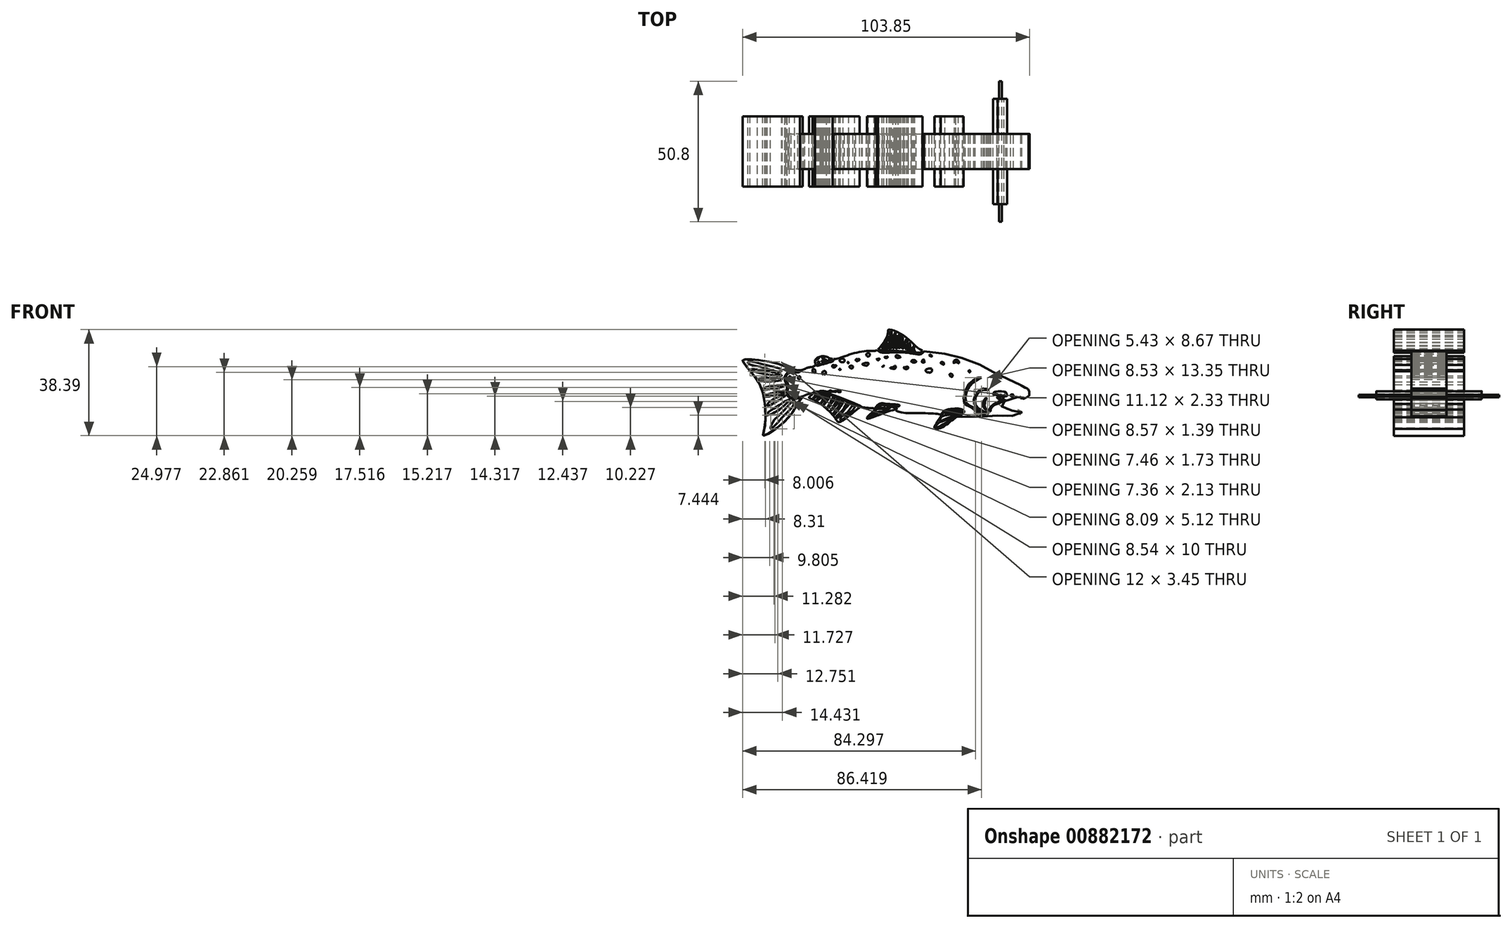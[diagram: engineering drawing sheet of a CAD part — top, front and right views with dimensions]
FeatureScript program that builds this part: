
annotation { "Feature Type Name" : "Feature", "Feature Type Description" : "" }
export const myFeature = defineFeature(function(context is Context, id is Id, definition is map)
    precondition{}
    {
        {
            var Q0;
            Q0=qCreatedBy(makeId("Front.planeOp"),FACE);
            var sketch = newSketch(context, id + "F0", { "sketchPlane" : qUnion([Q0])});
            skFitSpline(sketch, "E0", {"points": [v(-126.3, 57.16) * mm, v(-122.53, 51.96) * mm, v(-118.96, 45.5) * mm, v(-118.32, 32.67) * mm, v(-118.83, 29.86) * mm, v(-114.86, 31.9) * mm, v(-108.2, 38.29) * mm, v(-103.96, 44.3) * mm, v(-100.92, 44.95) * mm, v(-102.26, 43.7) * mm, v(-100.62, 42.85) * mm, v(-92.77, 36.26) * mm, v(-91.17, 34.8) * mm, v(-83.94, 40.08) * mm, v(-83.18, 40.16) * mm, v(-78.63, 39.71) * mm, v(-78.28, 39.56) * mm, v(-81.34, 36.1) * mm, v(-71.88, 39.13) * mm, v(-69.43, 38.37) * mm, v(-54.86, 37.46) * mm, v(-55.12, 35.97) * mm, v(-56.86, 32.59) * mm, v(-53.83, 33.01) * mm, v(-48.9, 36.64) * mm, v(-48.56, 36.58) * mm, v(-43.64, 36.74) * mm, v(-41.12, 37.23) * mm, v(-39, 36.68) * mm, v(-34.73, 37.16) * mm, v(-31.65, 36.82) * mm, v(-26.68, 37.33) * mm, v(-25.53, 37.66) * mm, v(-25.43, 38.9) * mm, v(-28.05, 39) * mm, v(-30.44, 39.16) * mm, v(-32.58, 40.43) * mm, v(-33.75, 41.28) * mm, v(-30.31, 42.82) * mm, v(-27.37, 44.06) * mm, v(-26.7, 43.54) * mm, v(-26.4, 43.85) * mm, v(-26.23, 43.54) * mm, v(-26.07, 43.6) * mm, v(-25.93, 43.87) * mm, v(-25.54, 43.76) * mm, v(-25.7, 43.55) * mm, v(-25.57, 43.34) * mm, v(-25.43, 43.29) * mm, v(-25.42, 43.53) * mm, v(-25.04, 43.51) * mm, v(-24.92, 43.25) * mm, v(-24.5, 43.23) * mm, v(-24.44, 43.36) * mm, v(-24.2, 43.37) * mm, v(-24.14, 43.56) * mm, v(-24.03, 43.54) * mm, v(-23.85, 43.56) * mm, v(-23.77, 43.75) * mm, v(-23.44, 43.71) * mm, v(-23.4, 43.9) * mm, v(-23.1, 43.92) * mm, v(-23.05, 44.05) * mm, v(-22.85, 44.1) * mm, v(-22.84, 44.24) * mm, v(-22.78, 44.3) * mm, v(-22.72, 44.39) * mm, v(-22.56, 44.46) * mm, v(-22.56, 44.68) * mm, v(-22.49, 44.73) * mm, v(-22.46, 45.17) * mm, v(-22.47, 45.89) * mm, v(-22.58, 45.95) * mm, v(-22.65, 46.15) * mm, v(-22.81, 46.18) * mm, v(-22.85, 46.49) * mm, v(-22.98, 46.5) * mm, v(-23.12, 46.57) * mm, v(-23.18, 46.78) * mm, v(-23.3, 46.81) * mm, v(-23.32, 46.9) * mm, v(-23.52, 46.9) * mm, v(-26.4, 48.49) * mm, v(-29.5, 49.94) * mm, v(-33.16, 51.55) * mm, v(-38.1, 54.14) * mm, v(-41.46, 56) * mm, v(-48.26, 58.33) * mm, v(-53.61, 59.55) * mm, v(-61.65, 60.79) * mm, v(-67.3, 65.55) * mm, v(-73.5, 68.17) * mm, v(-73.8, 66.6) * mm, v(-77.67, 60.8) * mm, v(-79.56, 60.56) * mm, v(-87.18, 59.3) * mm, v(-93.71, 57.6) * mm, v(-96.9, 58.57) * mm, v(-99.98, 57.26) * mm, v(-100.13, 55.18) * mm, v(-102.83, 54.44) * mm, v(-103.97, 53.88) * mm, v(-106.77, 53.53) * mm, v(-110.98, 54.97) * mm, v(-115.33, 56.3) * mm, v(-118.88, 56.97) * mm, v(-122.25, 57.44) * mm, v(-125.65, 57.42) * mm, v(-126.3, 57.16) * mm]});
            skFitSpline(sketch, "E1", {"points": [v(-38.58, 42.2) * mm, v(-38.49, 42.7) * mm, v(-38.1, 43.23) * mm, v(-37.98, 43.46) * mm, v(-38.38, 43.35) * mm, v(-38.98, 42.75) * mm, v(-39.22, 42.08) * mm, v(-39.2, 40.97) * mm, v(-39.1, 40.03) * mm, v(-38.17, 39.18) * mm, v(-38.49, 39.94) * mm, v(-38.76, 40.68) * mm, v(-38.58, 42.2) * mm]});
            skFitSpline(sketch, "E2", {"points": [v(-37.16, 46.3) * mm, v(-39.3, 46.36) * mm, v(-41.74, 44.47) * mm, v(-41.92, 40.86) * mm, v(-39.88, 39.09) * mm, v(-38.6, 38.48) * mm, v(-37.7, 38.32) * mm, v(-37.62, 38.02) * mm, v(-39.66, 38.32) * mm, v(-41.25, 39.6) * mm, v(-42.6, 41.38) * mm, v(-41.96, 44.9) * mm, v(-40.1, 46.6) * mm, v(-38.35, 46.85) * mm, v(-37.16, 46.3) * mm]});
            skFitSpline(sketch, "E3", {"points": [v(-39.88, 50.82) * mm, v(-40.55, 51.03) * mm, v(-43.3, 49.52) * mm, v(-44.8, 48.01) * mm, v(-46.42, 42.9) * mm, v(-45.74, 41.07) * mm, v(-44.83, 40.7) * mm, v(-42.84, 39.42) * mm, v(-40.61, 37.62) * mm, v(-38.38, 37.26) * mm, v(-37.5, 37.65) * mm, v(-38.75, 37.68) * mm, v(-40.64, 38.54) * mm, v(-42.96, 40.13) * mm, v(-44.98, 41.26) * mm, v(-45.71, 43.12) * mm, v(-44.98, 46.51) * mm, v(-43.48, 48.53) * mm, v(-41.62, 49.9) * mm, v(-39.88, 50.82) * mm]});
            skFitSpline(sketch, "E4", {"points": [v(-37.1, 38.61) * mm, v(-37.12, 39.43) * mm, v(-34.7, 41.75) * mm, v(-32.67, 42.41) * mm, v(-31.6, 42.72) * mm, v(-31.15, 42.7) * mm, v(-32.34, 42.16) * mm, v(-33.8, 41.49) * mm, v(-35.73, 40.56) * mm, v(-36.66, 39.1) * mm, v(-36.53, 38.8) * mm, v(-37.1, 38.61) * mm]});
            skFitSpline(sketch, "E5", {"points": [v(-29.1, 44.75) * mm, v(-28.44, 44.73) * mm, v(-28.4, 44.23) * mm, v(-28.76, 44.16) * mm, v(-28.87, 44.07) * mm, v(-29.04, 44.1) * mm, v(-29.14, 44.13) * mm, v(-29.34, 44.2) * mm, v(-29.36, 44.47) * mm, v(-29.3, 44.58) * mm, v(-29.21, 44.72) * mm, v(-29.1, 44.75) * mm]});
            skFitSpline(sketch, "E6", {"points": [v(-103.96, 44.3) * mm, v(-106.66, 43.53) * mm, v(-108.49, 43.51) * mm, v(-110, 45.35) * mm, v(-109.72, 48.08) * mm, v(-110.7, 50.66) * mm, v(-108.97, 52.64) * mm, v(-105.58, 52.9) * mm, v(-105.38, 53.52) * mm], "startDerivative": vector(-21.58, -8.13) * mm, "endDerivative": vector(2.14, 13) * mm});
            skFitSpline(sketch, "E7", {"points": [v(-46.3, 46.77) * mm, v(-48.8, 47.03) * mm, v(-58.6, 48.53) * mm, v(-70.23, 50.53) * mm, v(-80.9, 51.4) * mm, v(-90.28, 51.18) * mm, v(-99.57, 50) * mm, v(-109.34, 47.93) * mm], "startDerivative": vector(-27.18, 2.36) * mm, "endDerivative": vector(-64.33, -14.79) * mm});
            skFitSpline(sketch, "E8.0", {"points": [v(-46.24, 47.43) * mm, v(-46.52, 47.45) * mm, v(-46.94, 47.49) * mm, v(-47.59, 47.55) * mm, v(-48.13, 47.61) * mm, v(-48.77, 47.69) * mm, v(-49.51, 47.78) * mm, v(-50.35, 47.9) * mm, v(-51.57, 48.07) * mm, v(-53.27, 48.32) * mm, v(-55.49, 48.67) * mm, v(-57.78, 49.05) * mm, v(-60.05, 49.45) * mm, v(-62.28, 49.86) * mm, v(-64.47, 50.26) * mm, v(-66.65, 50.64) * mm, v(-68.8, 51) * mm, v(-70.97, 51.3) * mm, v(-73.85, 51.64) * mm, v(-77.42, 51.93) * mm, v(-81.6, 52.1) * mm, v(-85.6, 52.1) * mm, v(-89.55, 51.92) * mm, v(-93.49, 51.57) * mm, v(-97.44, 51.06) * mm, v(-101.44, 50.36) * mm, v(-105.46, 49.5) * mm, v(-108.14, 48.89) * mm, v(-109.48, 48.58) * mm]});
            skFitSpline(sketch, "E9", {"points": [v(-109.48, 48.58) * mm, v(-109.8, 48.45) * mm, v(-109.72, 48.08) * mm, v(-109.61, 47.87) * mm, v(-109.34, 47.93) * mm], "startDerivative": vector(-1.46, -0.57) * mm, "endDerivative": vector(1.35, 0.59) * mm});
            skFitSpline(sketch, "E10", {"points": [v(-46.24, 47.43) * mm, v(-45.9, 47.33) * mm, v(-45.99, 47.05) * mm, v(-46.07, 46.8) * mm, v(-46.3, 46.77) * mm, v(-46.34, 46.77) * mm], "startDerivative": vector(1.71, -0.53) * mm, "endDerivative": vector(-0.34, 0.06) * mm});
            skFitSpline(sketch, "E11", {"points": [v(-105.47, 53.51) * mm, v(-105.56, 53.51) * mm, v(-105.86, 53.22) * mm, v(-108.84, 53.08) * mm, v(-110.7, 51.89) * mm, v(-111.1, 50.53) * mm, v(-110.73, 49.16) * mm, v(-110.35, 48.23) * mm, v(-110.3, 47.75) * mm, v(-110.26, 46.94) * mm, v(-110.39, 45.79) * mm, v(-110.28, 45.1) * mm, v(-110.1, 44.3) * mm, v(-109.43, 43.68) * mm, v(-108.56, 43.12) * mm, v(-107.6, 43.12) * mm, v(-106.63, 43.22) * mm, v(-105.48, 43.51) * mm, v(-104.82, 43.72) * mm, v(-103.96, 44.3) * mm, v(-103.92, 44.33) * mm], "startDerivative": vector(-2.14, -10.83) * mm, "endDerivative": vector(6.68, 2.02) * mm});
            skArc(sketch, "E12", {"start": v(-33.68, 44.86) * mm, "mid": v(-33.1, 43.25) * mm, "end": v(-32.17, 44.67) * mm});
            skCircle(sketch, "E13", {"center": v(-33, 44.2) * mm, "radius": 0.48 * mm});
            skFitSpline(sketch, "E14", {"points": [v(-100, 55.57) * mm, v(-99.36, 55.18) * mm, v(-97.87, 55.47) * mm, v(-96.69, 55.84) * mm, v(-95.63, 56.09) * mm, v(-94.29, 56.52) * mm, v(-93.52, 56.84) * mm, v(-93.37, 57.58) * mm], "startDerivative": vector(3.3, -0.78) * mm, "endDerivative": vector(0.48, 7.3) * mm});
            skFitSpline(sketch, "E15", {"points": [v(-77.32, 61.06) * mm, v(-75.5, 60.6) * mm, v(-72.52, 60.6) * mm, v(-69.2, 60.41) * mm, v(-65.58, 60.2) * mm, v(-63.48, 59.95) * mm, v(-61.86, 60) * mm, v(-61.26, 60.62) * mm], "startDerivative": vector(10.67, 0.5) * mm, "endDerivative": vector(6, 2.75) * mm});
            skFitSpline(sketch, "E16", {"points": [v(-100.92, 44.95) * mm, v(-99.22, 45.37) * mm, v(-97.18, 45.33) * mm, v(-87.3, 41.65) * mm, v(-83.94, 40.08) * mm], "startDerivative": vector(10.53, 2.85) * mm, "endDerivative": vector(10.65, -5.4) * mm});
            skFitSpline(sketch, "E17", {"points": [v(-101.29, 45.12) * mm, v(-101.19, 45.45) * mm, v(-100.62, 45.46) * mm, v(-100.6, 45.72) * mm, v(-99.5, 45.8) * mm, v(-98.21, 45.9) * mm, v(-98.18, 46.06) * mm, v(-97.09, 46.03) * mm, v(-97.07, 46.25) * mm, v(-96.94, 46.22) * mm, v(-96.83, 46.01) * mm, v(-94.9, 45.96) * mm, v(-94.63, 46.27) * mm, v(-94.42, 46.03) * mm, v(-93.02, 46.04) * mm, v(-90.78, 46.04) * mm, v(-90.77, 45.62) * mm, v(-91.48, 45.6) * mm, v(-91.83, 45.83) * mm, v(-92.58, 45.74) * mm, v(-92.76, 45.67) * mm, v(-94.95, 45.64) * mm, v(-94.92, 45.45) * mm, v(-95.91, 45.45) * mm, v(-94.03, 44.79) * mm, v(-88.5, 42.67) * mm, v(-84.29, 40.82) * mm, v(-83.18, 40.16) * mm], "startDerivative": vector(-0.84, 18.9) * mm, "endDerivative": vector(20.54, -13.82) * mm});
            skFitSpline(sketch, "E18", {"points": [v(-78.28, 39.56) * mm, v(-76.25, 41.18) * mm, v(-73.05, 40.87) * mm, v(-70.15, 40.6) * mm, v(-71.52, 40.48) * mm, v(-72.01, 40.19) * mm, v(-71.01, 39.69) * mm, v(-71.57, 39.16) * mm], "startDerivative": vector(10.5, 11.86) * mm, "endDerivative": vector(-10.11, -5.79) * mm});
            skFitSpline(sketch, "E19", {"points": [v(-54.63, 36.8) * mm, v(-53.8, 37.9) * mm, v(-52.68, 38.76) * mm, v(-50.95, 39.24) * mm, v(-49, 39.34) * mm, v(-47.7, 39.24) * mm, v(-46.82, 38.93) * mm, v(-46.4, 38.47) * mm, v(-47.11, 37.72) * mm, v(-47.98, 37.26) * mm, v(-48.86, 36.86) * mm, v(-49.23, 36.61) * mm, v(-49.21, 36.45) * mm], "startDerivative": vector(8.95, 11.53) * mm, "endDerivative": vector(0.27, -3.63) * mm});
            skFitSpline(sketch, "E20", {"points": [v(-78.5, 39.7) * mm, v(-76.55, 41.5) * mm, v(-73.88, 41.34) * mm, v(-69.54, 40.85) * mm, v(-70.03, 40.39) * mm, v(-71.4, 40.2) * mm, v(-70.59, 39.85) * mm, v(-71.02, 39.1) * mm], "startDerivative": vector(10.06, 13.32) * mm, "endDerivative": vector(-8.89, -8.33) * mm});
            skFitSpline(sketch, "E21", {"points": [v(-100, 55.82) * mm, v(-99.3, 55.4) * mm, v(-96.78, 56.16) * mm, v(-94.3, 56.81) * mm, v(-93.71, 57.6) * mm], "startDerivative": vector(3.25, -3.36) * mm, "endDerivative": vector(2.08, 4.52) * mm});
            skFitSpline(sketch, "E22", {"points": [v(-77.67, 60.8) * mm, v(-76.11, 59.97) * mm, v(-71.39, 59.97) * mm, v(-65.63, 59.68) * mm, v(-61.77, 59.36) * mm, v(-60.74, 60.43) * mm], "startDerivative": vector(8.9, -6.7) * mm, "endDerivative": vector(5.78, 9.9) * mm});
            skFitSpline(sketch, "E23", {"points": [v(-34.2, 44.5) * mm, v(-34, 44.87) * mm, v(-34.68, 44.87) * mm, v(-35.3, 44.53) * mm, v(-35.71, 44.73) * mm, v(-35.54, 45.32) * mm, v(-34.09, 45.88) * mm, v(-31.4, 45.66) * mm, v(-30.7, 44.95) * mm, v(-30.75, 44.14) * mm, v(-31.14, 44.05) * mm, v(-31.67, 44.67) * mm, v(-31.7, 44.17) * mm, v(-32.07, 43.21) * mm, v(-33.29, 43) * mm, v(-34.24, 43.8) * mm, v(-34.2, 44.5) * mm]});
            skFitSpline(sketch, "E24", {"points": [v(-33.8, 44.95) * mm, v(-34.13, 45.11) * mm, v(-34.82, 45.02) * mm, v(-34.98, 44.87) * mm, v(-35.25, 44.87) * mm, v(-35.36, 44.7) * mm, v(-35.55, 44.87) * mm, v(-35.35, 45.11) * mm, v(-35, 45.15) * mm, v(-34.98, 45.33) * mm, v(-34.7, 45.34) * mm, v(-34.63, 45.52) * mm, v(-33.8, 45.48) * mm, v(-33.64, 45.72) * mm, v(-32.66, 45.68) * mm, v(-32.62, 45.49) * mm, v(-31.93, 45.49) * mm, v(-31.9, 45.34) * mm, v(-31.7, 45.34) * mm, v(-31.65, 45.14) * mm, v(-31.4, 45.17) * mm, v(-31.22, 45.04) * mm, v(-31.05, 44.8) * mm, v(-31.02, 44.22) * mm, v(-31.37, 44.7) * mm, v(-31.69, 44.87) * mm, v(-31.95, 44.87) * mm, v(-32.01, 44.8) * mm, v(-32.02, 44.7) * mm, v(-32.17, 44.67) * mm], "startDerivative": vector(-7, 5.33) * mm, "endDerivative": vector(-7.82, -0.11) * mm});
            skFitSpline(sketch, "E25", {"points": [v(-33.8, 44.95) * mm, v(-33.68, 44.86) * mm], "startDerivative": vector(0.12, -0.1) * mm, "endDerivative": vector(0.12, -0.1) * mm});
            skFitSpline(sketch, "E26", {"points": [v(-118.23, 53.42) * mm, v(-123.5, 53.8) * mm, v(-121.54, 52.85) * mm, v(-112.09, 51.59) * mm, v(-114.17, 52.43) * mm, v(-118.23, 53.42) * mm]});
            skFitSpline(sketch, "E27", {"points": [v(-116.24, 50.78) * mm, v(-118.52, 50.78) * mm, v(-119.83, 50.64) * mm, v(-120.96, 50.28) * mm, v(-119.08, 49.5) * mm, v(-112.87, 49.82) * mm, v(-112.11, 50.19) * mm, v(-111.9, 50.46) * mm, v(-116.24, 50.78) * mm]});
            skFitSpline(sketch, "E28", {"points": [v(-111.76, 48.2) * mm, v(-114.2, 47.98) * mm, v(-117.64, 47.44) * mm, v(-118.93, 46.59) * mm, v(-116.68, 46.62) * mm, v(-114.78, 47) * mm, v(-111.82, 47.52) * mm, v(-111.05, 48.19) * mm, v(-111.76, 48.2) * mm]});
            skFitSpline(sketch, "E29", {"points": [v(-111.1, 46.11) * mm, v(-116.9, 44.89) * mm, v(-118.24, 44.2) * mm, v(-117, 43.98) * mm, v(-112.86, 45) * mm, v(-110.97, 45.5) * mm, v(-110.76, 46) * mm, v(-111.1, 46.11) * mm]});
            skFitSpline(sketch, "E30", {"points": [v(-110.73, 44.58) * mm, v(-116.46, 42.24) * mm, v(-117.23, 40.74) * mm, v(-112.82, 42.91) * mm, v(-110.73, 44.58) * mm]});
            skFitSpline(sketch, "E31", {"points": [v(-110.3, 42.62) * mm, v(-113.76, 40.45) * mm, v(-117.1, 38.2) * mm, v(-117.62, 37.23) * mm, v(-116, 37.65) * mm, v(-114.23, 38.49) * mm, v(-110.1, 41.8) * mm, v(-109.39, 42.92) * mm, v(-110.3, 42.62) * mm]});
            skFitSpline(sketch, "E32", {"points": [v(-108.22, 42.27) * mm, v(-112.22, 38.12) * mm, v(-114, 36.4) * mm, v(-115.09, 35.21) * mm, v(-116.16, 32.3) * mm, v(-110.94, 37.43) * mm, v(-107.9, 40.9) * mm, v(-107.51, 42.7) * mm, v(-108.22, 42.27) * mm]});
            skFitSpline(sketch, "E33", {"points": [v(-124.29, 56.53) * mm, v(-124.2, 55.91) * mm, v(-120.81, 54.96) * mm, v(-112.33, 53.05) * mm, v(-112.36, 53.7) * mm, v(-117.31, 55.3) * mm, v(-124.29, 56.53) * mm]});
            skFitSpline(sketch, "E34", {"points": [v(-99.61, 44.73) * mm, v(-100.45, 43.93) * mm, v(-100.8, 43.35) * mm, v(-98.48, 44.9) * mm, v(-99.61, 44.73) * mm]});
            skFitSpline(sketch, "E35", {"points": [v(-98.06, 44.83) * mm, v(-98.55, 43.93) * mm, v(-99.7, 42.57) * mm, v(-98.8, 42.88) * mm, v(-97.5, 44.08) * mm, v(-97.24, 44.84) * mm, v(-97.66, 45.04) * mm, v(-98.06, 44.83) * mm]});
            skFitSpline(sketch, "E36", {"points": [v(-96.39, 44.74) * mm, v(-96.76, 44.49) * mm, v(-96.9, 43.95) * mm, v(-97.86, 41.54) * mm, v(-96.16, 44.34) * mm, v(-96.39, 44.74) * mm]});
            skFitSpline(sketch, "E37", {"points": [v(-95.34, 44.2) * mm, v(-95.8, 43.25) * mm, v(-96.98, 40.94) * mm, v(-94.81, 44.02) * mm, v(-95.34, 44.2) * mm]});
            skFitSpline(sketch, "E38", {"points": [v(-93.6, 43.62) * mm, v(-94.47, 42.1) * mm, v(-95.64, 39.72) * mm, v(-93, 43.6) * mm, v(-93.6, 43.62) * mm]});
            skFitSpline(sketch, "E39", {"points": [v(-92.06, 43.27) * mm, v(-92.54, 42.02) * mm, v(-94.54, 38.7) * mm, v(-91.42, 42.8) * mm, v(-92.06, 43.27) * mm]});
            skFitSpline(sketch, "E40", {"points": [v(-90.76, 42.44) * mm, v(-90.95, 41.47) * mm, v(-93.59, 37.59) * mm, v(-93.32, 37.32) * mm, v(-90.86, 40.32) * mm, v(-90.08, 41.48) * mm, v(-90.08, 42.44) * mm, v(-90.76, 42.44) * mm]});
            skFitSpline(sketch, "E41", {"points": [v(-89.14, 40.58) * mm, v(-91.79, 37.46) * mm, v(-92.55, 36.58) * mm, v(-92.05, 36.26) * mm, v(-89.3, 39.48) * mm, v(-87.86, 41.25) * mm, v(-88.3, 41.72) * mm, v(-89.14, 40.58) * mm]});
            skFitSpline(sketch, "E42", {"points": [v(-86, 40.83) * mm, v(-87.03, 40.12) * mm, v(-87.98, 38.76) * mm, v(-89.68, 37.26) * mm, v(-90.92, 36.26) * mm, v(-90.77, 35.51) * mm, v(-87.52, 38.09) * mm, v(-85.7, 40.33) * mm, v(-86, 40.83) * mm]});
            skFitSpline(sketch, "E43", {"points": [v(-99.11, 56.53) * mm, v(-98.98, 56.12) * mm, v(-99.06, 55.91) * mm, v(-98.84, 55.88) * mm, v(-98.53, 56.08) * mm, v(-98.66, 56.63) * mm, v(-99.11, 56.53) * mm]});
            skFitSpline(sketch, "E44", {"points": [v(-97.42, 57.22) * mm, v(-97.5, 56.95) * mm, v(-97.8, 56.77) * mm, v(-97.42, 56.64) * mm, v(-96.9, 56.73) * mm, v(-96.7, 56.92) * mm, v(-97.05, 57.11) * mm, v(-97.42, 57.22) * mm]});
            skFitSpline(sketch, "E45", {"points": [v(-96.41, 57.27) * mm, v(-96.04, 57.3) * mm, v(-96, 57.06) * mm, v(-95.8, 57.07) * mm, v(-95.8, 56.91) * mm, v(-95.82, 56.76) * mm, v(-96.42, 56.76) * mm, v(-96.41, 57.27) * mm]});
            skFitSpline(sketch, "E46", {"points": [v(-94.9, 57.3) * mm, v(-95.16, 57.27) * mm, v(-95.22, 56.97) * mm, v(-95.17, 56.75) * mm, v(-95.02, 56.73) * mm, v(-95.02, 56.98) * mm, v(-94.85, 57.03) * mm, v(-94.8, 57.28) * mm, v(-94.9, 57.3) * mm]});
            skFitSpline(sketch, "E47", {"points": [v(-109, 51.25) * mm, v(-109.52, 51.2) * mm, v(-109.31, 50.85) * mm, v(-108.75, 50.91) * mm, v(-109, 51.25) * mm]});
            skFitSpline(sketch, "E48", {"points": [v(-100.95, 52.84) * mm, v(-100.95, 53.16) * mm, v(-100.79, 54.04) * mm, v(-99.88, 53.29) * mm, v(-100, 53.01) * mm, v(-99.95, 52.7) * mm, v(-100.95, 52.84) * mm]});
            skFitSpline(sketch, "E49", {"points": [v(-84.45, 57.63) * mm, v(-85.16, 57.53) * mm, v(-85.4, 57.1) * mm, v(-84.74, 56.83) * mm, v(-83.97, 57.42) * mm, v(-84.45, 57.63) * mm]});
            skFitSpline(sketch, "E50", {"points": [v(-69.8, 58.75) * mm, v(-70.36, 58.96) * mm, v(-70.82, 58.85) * mm, v(-70.8, 58.18) * mm, v(-69.73, 58.05) * mm, v(-69.12, 58.28) * mm, v(-69.8, 58.75) * mm]});
            skFitSpline(sketch, "E51", {"points": [v(-50.39, 51.84) * mm, v(-51.02, 52.21) * mm, v(-51.44, 51.98) * mm, v(-50.97, 51.25) * mm, v(-50.53, 51.12) * mm, v(-50.39, 51.84) * mm]});
            skFitSpline(sketch, "E52", {"points": [v(-60.57, 56.75) * mm, v(-60.72, 57.36) * mm, v(-61.14, 57.21) * mm, v(-61.4, 56.4) * mm, v(-60.55, 56.37) * mm, v(-60.57, 56.75) * mm]});
            skFitSpline(sketch, "E53", {"points": [v(-93.23, 55.34) * mm, v(-92.4, 55.27) * mm, v(-92.83, 54.67) * mm, v(-93.78, 54.7) * mm, v(-93.73, 55.32) * mm, v(-93.23, 55.34) * mm]});
            skFitSpline(sketch, "E54", {"points": [v(-77.3, 57.64) * mm, v(-76.72, 57.67) * mm, v(-76.97, 57.27) * mm, v(-77.37, 57.12) * mm, v(-77.77, 57.57) * mm, v(-77.3, 57.64) * mm]});
            skFitSpline(sketch, "E55", {"points": [v(-67.16, 54.7) * mm, v(-67.86, 54.7) * mm, v(-67.96, 54.27) * mm, v(-67.16, 53.92) * mm, v(-66.38, 54.3) * mm, v(-66.56, 54.82) * mm, v(-67.16, 54.7) * mm]});
            skFitSpline(sketch, "E56", {"points": [v(-54.1, 56.52) * mm, v(-54.6, 56.34) * mm, v(-54.6, 56.09) * mm, v(-53.6, 55.54) * mm, v(-53.45, 56.09) * mm, v(-54.1, 56.52) * mm]});
            skFitSpline(sketch, "E57", {"points": [v(-43.98, 53.3) * mm, v(-44.36, 53.52) * mm, v(-44.53, 53.1) * mm, v(-44.13, 52.77) * mm, v(-43.98, 53.3) * mm]});
            skFitSpline(sketch, "E58", {"points": [v(-75.73, 54.78) * mm, v(-75.5, 54.78) * mm, v(-75.13, 55.2) * mm, v(-75.73, 54.78) * mm]});
            skFitSpline(sketch, "E59", {"points": [v(-86.6, 55.14) * mm, v(-87.67, 54.78) * mm, v(-86.66, 54.19) * mm, v(-86.6, 55.14) * mm]});
            skFitSpline(sketch, "E60", {"points": [v(-105.78, 51.3) * mm, v(-106.29, 50.85) * mm, v(-105.82, 50.26) * mm, v(-105.4, 51.06) * mm, v(-105.78, 51.3) * mm]});
            skFitSpline(sketch, "E61", {"points": [v(-89.64, 57.6) * mm, v(-90.77, 57.6) * mm, v(-91.27, 57.2) * mm, v(-90.77, 56.57) * mm, v(-89.55, 56.66) * mm, v(-89.64, 57.6) * mm]});
            skFitSpline(sketch, "E62", {"points": [v(-58.17, 59.05) * mm, v(-58.76, 59) * mm, v(-58.26, 58.57) * mm, v(-57.84, 58.57) * mm, v(-58.17, 59.05) * mm]});
            skFitSpline(sketch, "E63", {"points": [v(-57.92, 54.04) * mm, v(-59.98, 53.68) * mm, v(-59.9, 53) * mm, v(-58.93, 52.7) * mm, v(-58.05, 52.88) * mm, v(-57.92, 54.04) * mm]});
            skFitSpline(sketch, "E64", {"points": [v(-82.91, 55.78) * mm, v(-80.77, 56.09) * mm, v(-81.19, 55.27) * mm, v(-82.15, 55.31) * mm, v(-82.91, 55.78) * mm]});
            skFitSpline(sketch, "E65", {"points": [v(-48.3, 57) * mm, v(-49.77, 57.04) * mm, v(-49.86, 56.09) * mm, v(-49.1, 56.45) * mm, v(-48.1, 56.09) * mm, v(-48.3, 57) * mm]});
            skFitSpline(sketch, "E66", {"points": [v(-71.6, 54.78) * mm, v(-72.93, 54.35) * mm, v(-71.68, 54.04) * mm, v(-70.85, 54.43) * mm, v(-71.1, 55.2) * mm, v(-71.6, 54.78) * mm]});
            skFitSpline(sketch, "E67", {"points": [v(-80.42, 59.57) * mm, v(-81.4, 59.43) * mm, v(-81.27, 58.57) * mm, v(-80.49, 58.57) * mm, v(-80.42, 59.57) * mm]});
            skFitSpline(sketch, "E68", {"points": [v(-96.86, 53.22) * mm, v(-97.36, 53.02) * mm, v(-97.48, 52.82) * mm, v(-97.36, 52.3) * mm, v(-97.53, 52.14) * mm, v(-97.18, 52.04) * mm, v(-96.9, 52.22) * mm, v(-96.58, 52) * mm, v(-96.33, 52.12) * mm, v(-96.16, 52.62) * mm, v(-96.33, 53.12) * mm, v(-96.86, 53.22) * mm]});
            skFitSpline(sketch, "E69", {"points": [v(-99.17, 57.48) * mm, v(-98.69, 57.78) * mm, v(-99.28, 57.78) * mm, v(-99.61, 57.19) * mm, v(-99.17, 57.48) * mm]});
            skFitSpline(sketch, "E70", {"points": [v(-96.65, 58.05) * mm, v(-97.42, 58.24) * mm, v(-97.6, 58.05) * mm, v(-97.42, 57.8) * mm, v(-97.16, 57.78) * mm, v(-96.65, 58.05) * mm]});
            skFitSpline(sketch, "E71", {"points": [v(-91.08, 54.08) * mm, v(-91.33, 53.9) * mm, v(-91.33, 53.73) * mm, v(-91.2, 53.64) * mm, v(-90.96, 53.6) * mm, v(-90.86, 53.74) * mm, v(-90.92, 54) * mm, v(-91.08, 54.08) * mm]});
            skFitSpline(sketch, "E72", {"points": [v(-88.1, 56.52) * mm, v(-88.26, 56.52) * mm, v(-88.29, 56.41) * mm, v(-88.25, 56.22) * mm, v(-88.05, 56.01) * mm, v(-87.9, 56.11) * mm, v(-87.97, 56.26) * mm, v(-87.98, 56.38) * mm, v(-88.1, 56.52) * mm]});
            skFitSpline(sketch, "E73", {"points": [v(-74.43, 58.28) * mm, v(-73.88, 58.47) * mm, v(-73.83, 58.17) * mm, v(-74.56, 57.93) * mm, v(-74.9, 58.33) * mm, v(-74.43, 58.28) * mm]});
            skFitSpline(sketch, "E74", {"points": [v(-64.34, 57.22) * mm, v(-65.29, 56.77) * mm, v(-64.7, 56.35) * mm, v(-63.5, 56.59) * mm, v(-64.34, 57.22) * mm]});
            skFitSpline(sketch, "E75", {"points": [v(-75.6, 61.19) * mm, v(-75.73, 62.29) * mm, v(-75.53, 62.51) * mm, v(-75.46, 62.16) * mm, v(-75.23, 61.09) * mm, v(-75.6, 61.19) * mm]});
            skFitSpline(sketch, "E76", {"points": [v(-73.36, 65.54) * mm, v(-74.1, 65.04) * mm, v(-73.36, 61.46) * mm, v(-72.86, 61.15) * mm, v(-73.3, 64.35) * mm, v(-73.36, 65.54) * mm]});
            skFitSpline(sketch, "E77", {"points": [v(-72.83, 67.63) * mm, v(-71.94, 61.49) * mm, v(-71.61, 61.54) * mm, v(-71.6, 62.07) * mm, v(-71.76, 63.61) * mm, v(-72.4, 66.55) * mm, v(-72.49, 67.73) * mm, v(-72.83, 67.63) * mm]});
            skFitSpline(sketch, "E78", {"points": [v(-71.19, 67.1) * mm, v(-71.45, 64.4) * mm, v(-71.01, 61.93) * mm, v(-70.81, 61.4) * mm, v(-70.46, 61.41) * mm, v(-70.38, 61.96) * mm, v(-70.55, 63.82) * mm, v(-70.95, 66.55) * mm, v(-70.93, 67.1) * mm, v(-71.19, 67.1) * mm]});
            skFitSpline(sketch, "E79", {"points": [v(-69.39, 66.18) * mm, v(-69.7, 66.27) * mm, v(-69.93, 66.17) * mm, v(-70.05, 64.9) * mm, v(-69.83, 61.66) * mm, v(-69.33, 61.51) * mm, v(-69.29, 62.97) * mm, v(-69.53, 65.12) * mm, v(-69.39, 66.18) * mm]});
            skFitSpline(sketch, "E80", {"points": [v(-68.37, 64.77) * mm, v(-68.44, 65.67) * mm, v(-68.7, 65.65) * mm, v(-68.68, 61.58) * mm, v(-68.19, 61.37) * mm, v(-68.1, 63.1) * mm, v(-68.37, 64.77) * mm]});
            skFitSpline(sketch, "E81", {"points": [v(-67.02, 64.82) * mm, v(-67.5, 61.57) * mm, v(-66.78, 60.86) * mm, v(-66.87, 63.35) * mm, v(-66.6, 64.58) * mm, v(-67.02, 64.82) * mm]});
            skFitSpline(sketch, "E82", {"points": [v(-65.64, 61.96) * mm, v(-65.8, 63.5) * mm, v(-66.14, 63.13) * mm, v(-65.98, 60.67) * mm, v(-65.23, 60.67) * mm, v(-65.64, 61.96) * mm]});
            skFitSpline(sketch, "E83", {"points": [v(-64.24, 62.3) * mm, v(-64.52, 62.14) * mm, v(-64.63, 61.9) * mm, v(-64.69, 61.1) * mm, v(-64.63, 60.44) * mm, v(-64.07, 60.37) * mm, v(-64.28, 61.33) * mm, v(-64.24, 62.3) * mm]});
            skFitSpline(sketch, "E84", {"points": [v(-75.12, 63.5) * mm, v(-74.77, 63.64) * mm, v(-74.7, 63.24) * mm, v(-74.3, 62.18) * mm, v(-74.08, 61.02) * mm, v(-74.66, 61.03) * mm, v(-74.86, 61.83) * mm, v(-75.12, 63.5) * mm]});
            skFitSpline(sketch, "E85", {"points": [v(-54.68, 37.31) * mm, v(-54.14, 38.06) * mm, v(-53.04, 38.97) * mm, v(-51.07, 39.53) * mm, v(-49.05, 39.63) * mm, v(-47.56, 39.54) * mm, v(-46.5, 39.06) * mm, v(-46.03, 38.58) * mm, v(-46.26, 38.15) * mm, v(-47.11, 37.49) * mm, v(-48.03, 37) * mm, v(-48.76, 36.65) * mm], "startDerivative": vector(7.36, 7.8) * mm, "endDerivative": vector(-9.33, -4.38) * mm});
            skFitSpline(sketch, "E86", {"points": [v(-46.8, 38.45) * mm, v(-48.97, 38.97) * mm, v(-51.95, 38.76) * mm, v(-53.1, 38) * mm, v(-48.76, 38.33) * mm, v(-46.8, 38.45) * mm]});
            skFitSpline(sketch, "E87", {"points": [v(-48.29, 37.9) * mm, v(-52.47, 36.03) * mm, v(-54.92, 35.22) * mm, v(-54.2, 36.7) * mm, v(-51.5, 37.38) * mm, v(-48.29, 37.9) * mm]});
            skFitSpline(sketch, "E88", {"points": [v(-49.7, 36.68) * mm, v(-53.55, 35.2) * mm, v(-55.58, 34.32) * mm, v(-56.41, 32.71) * mm, v(-49.7, 36.68) * mm]});
            skFitSpline(sketch, "E89", {"points": [v(-77.36, 37.85) * mm, v(-78.56, 37.85) * mm, v(-79.36, 37.8) * mm, v(-80.82, 36.52) * mm, v(-79.78, 36.74) * mm, v(-77.36, 37.85) * mm]});
            skFitSpline(sketch, "E90", {"points": [v(-73.12, 39.4) * mm, v(-75.05, 39.45) * mm, v(-77.59, 39.51) * mm, v(-78.36, 38.78) * mm, v(-78.72, 38.23) * mm, v(-77.05, 38.5) * mm, v(-75.61, 38.63) * mm, v(-73.12, 39.4) * mm]});
            skFitSpline(sketch, "E91", {"points": [v(-72.58, 40.38) * mm, v(-74.98, 40.81) * mm, v(-75.79, 40.95) * mm, v(-76.94, 40.12) * mm, v(-76.48, 39.95) * mm, v(-73.32, 39.85) * mm, v(-72.77, 39.97) * mm, v(-72.58, 40.38) * mm]});
            skSolve(sketch);
        }
        {
            var Q0;
            Q0=makeQuery(id+"F0.imprint","IMPRINT",FACE,{"disambiguationData":[TD([[makeQuery(id+"F0.imprint","IMPRINT",EDGE,{"derivedFrom":sQuery(id+"F0.wireOp",EDGE,"E1")}),-1.0]])]});
            var Q1;
            {var subQ0=sQuery(id+"F0.wireOp",EDGE,"E8.0");Q1=makeQuery(id+"F0.imprint","IMPRINT",FACE,{"disambiguationData":[TD([[makeQuery(id+"F0.imprint","IMPRINT",EDGE,{"derivedFrom":subQ0}),1.0]])]});}
            extrude(context, id + "F1", {"entities" : qUnion([Q0, Q1]), "endBound" : BoundingType.SYMMETRIC, "depth" : 12.7 * mm, "offsetDistance" : 25.4 * mm});
        }
        {
            var Q0;
            {var subQ0=sQuery(id+"F0.wireOp",EDGE,"E21");Q0=makeQuery(id+"F0.imprint","IMPRINT",FACE,{"disambiguationData":[TD([[makeQuery(id+"F0.imprint","IMPRINT",EDGE,{"derivedFrom":subQ0}),1.0]])]});}
            var Q1;
            {var subQ0=sQuery(id+"F0.wireOp",EDGE,"E15");Q1=makeQuery(id+"F0.imprint","IMPRINT",FACE,{"disambiguationData":[TD([[makeQuery(id+"F0.imprint","IMPRINT",EDGE,{"derivedFrom":subQ0}),1.0]])]});}
            var Q2;
            {var subQ0=sQuery(id+"F0.wireOp",EDGE,"E19");Q2=makeQuery(id+"F0.imprint","IMPRINT",FACE,{"disambiguationData":[TD([[makeQuery(id+"F0.imprint","IMPRINT",EDGE,{"derivedFrom":subQ0}),-1.0]])]});}
            var Q3;
            {var subQ0=sQuery(id+"F0.wireOp",EDGE,"E18");Q3=makeQuery(id+"F0.imprint","IMPRINT",FACE,{"disambiguationData":[TD([[makeQuery(id+"F0.imprint","IMPRINT",EDGE,{"derivedFrom":subQ0}),-1.0]])]});}
            var Q4;
            {var subQ0=sQuery(id+"F0.wireOp",EDGE,"E16");Q4=makeQuery(id+"F0.imprint","IMPRINT",FACE,{"disambiguationData":[TD([[makeQuery(id+"F0.imprint","IMPRINT",EDGE,{"derivedFrom":subQ0}),-1.0]])]});}
            var Q5;
            Q5=makeQuery(id+"F0.imprint","IMPRINT",FACE,{"disambiguationData":[TD([[makeQuery(id+"F0.imprint","IMPRINT",EDGE,{"derivedFrom":sQuery(id+"F0.wireOp",EDGE,"E26")}),-1.0]])]});
            extrude(context, id + "F2", {"entities" : qUnion([Q0, Q1, Q2, Q3, Q4, Q5]), "endBound" : BoundingType.SYMMETRIC, "depth" : 25.4 * mm, "offsetDistance" : 25.4 * mm});
        }
        {
            var Q0;
            Q0=makeQuery(id+"F0.imprint","IMPRINT",FACE,{"disambiguationData":[TD([[makeQuery(id+"F0.imprint","IMPRINT",EDGE,{"derivedFrom":sQuery(id+"F0.wireOp",EDGE,"E13")}),1.0]])]});
            extrude(context, id + "F3", {"entities" : qUnion([Q0]), "endBound" : BoundingType.SYMMETRIC, "depth" : 50.8 * mm, "offsetDistance" : 25.4 * mm});
        }
        {
            var Q0;
            Q0=makeQuery(id+"F0.imprint","IMPRINT",FACE,{"disambiguationData":[TD([[makeQuery(id+"F0.imprint","IMPRINT",EDGE,{"derivedFrom":sQuery(id+"F0.wireOp",EDGE,"E12")}),1.0]])]});
            var Q1;
            Q1=makeQuery(id+"F0.imprint","IMPRINT",FACE,{"disambiguationData":[TD([[makeQuery(id+"F0.imprint","IMPRINT",EDGE,{"derivedFrom":sQuery(id+"F0.wireOp",EDGE,"E12")}),-1.0]])]});
            extrude(context, id + "F4", {"entities" : qUnion([Q0, Q1]), "endBound" : BoundingType.SYMMETRIC, "depth" : 38.1 * mm, "offsetDistance" : 25.4 * mm});
        }
    });
